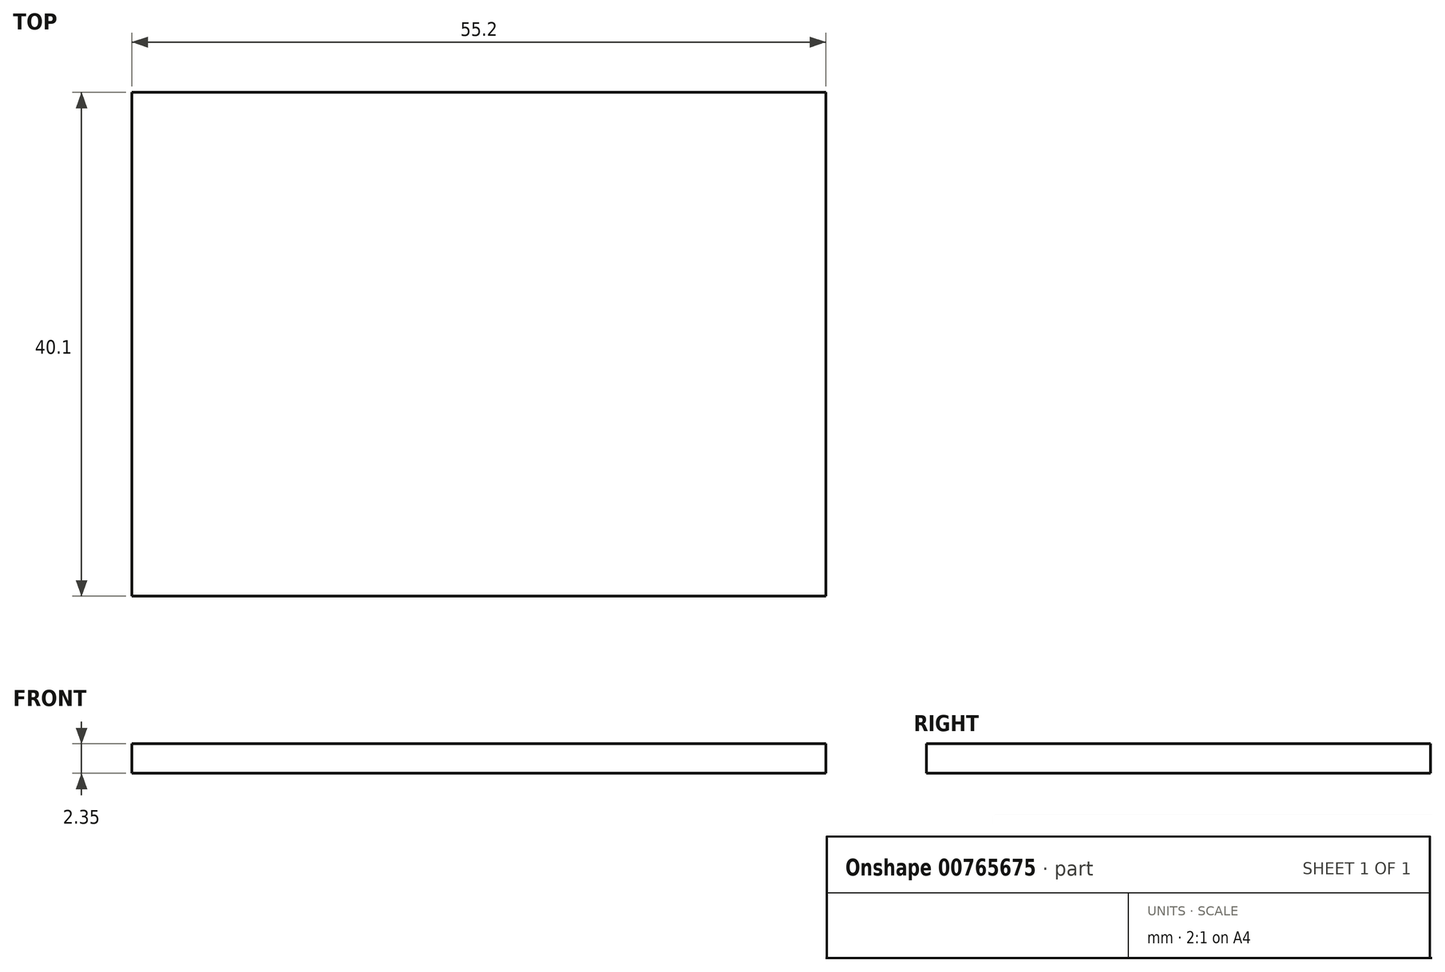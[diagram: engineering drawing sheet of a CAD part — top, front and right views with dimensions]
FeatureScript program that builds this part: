
annotation { "Feature Type Name" : "Feature", "Feature Type Description" : "" }
export const myFeature = defineFeature(function(context is Context, id is Id, definition is map)
    precondition{}
    {
        {
            var Q0;
            Q0=qCreatedBy(makeId("Top.planeOp"),FACE);
            var sketch = newSketch(context, id + "F0", { "sketchPlane" : qUnion([Q0])});
            skLineSegment(sketch, "E0.bottom", {"start": v(-26, 19.6) * mm, "end": v(29.2, 19.6) * mm});
            skLineSegment(sketch, "E0.top", {"start": v(-26, -20.5) * mm, "end": v(29.2, -20.5) * mm});
            skLineSegment(sketch, "E0.left", {"start": v(-26, 19.6) * mm, "end": v(-26, -20.5) * mm});
            skLineSegment(sketch, "E0.right", {"start": v(29.2, 19.6) * mm, "end": v(29.2, -20.5) * mm});
            skSolve(sketch);
        }
        {
            var Q0;
            Q0 = qSketchRegion(id + "F0", true);
            extrude(context, id + "F1", {"entities" : qUnion([Q0]), "depth" : 2.35 * mm, "offsetDistance" : 25.4 * mm});
        }
    });
